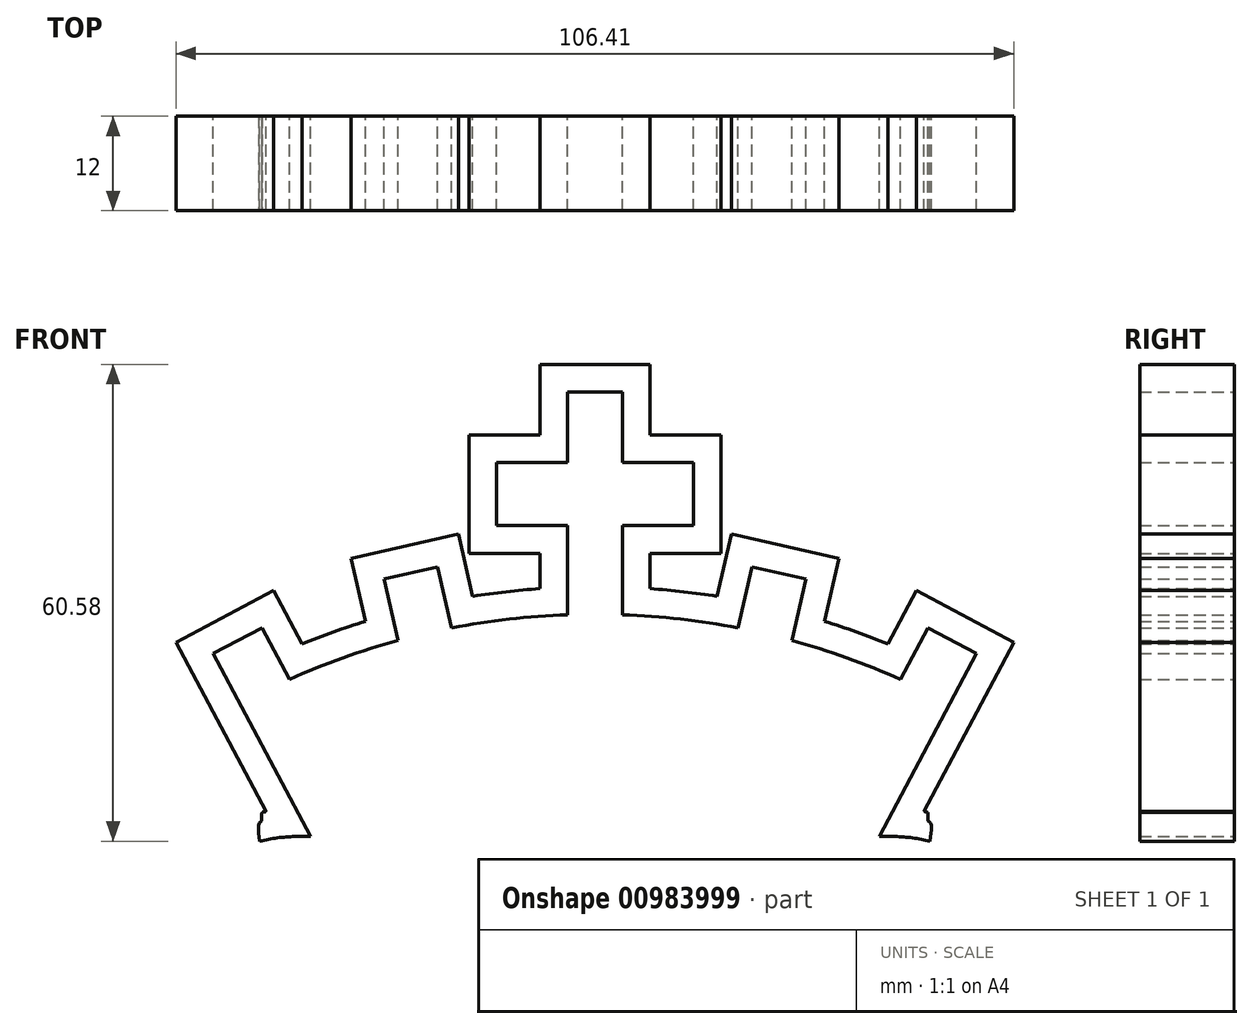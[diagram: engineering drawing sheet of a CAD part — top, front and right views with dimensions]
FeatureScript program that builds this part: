
annotation { "Feature Type Name" : "Feature", "Feature Type Description" : "" }
export const myFeature = defineFeature(function(context is Context, id is Id, definition is map)
    precondition{}
    {
        {
            var Q0;
            Q0=qCreatedBy(makeId("Front.planeOp"),FACE);
            var sketch = newSketch(context, id + "F0", { "sketchPlane" : qUnion([Q0])});
            skArc(sketch, "E0", {"start": v(-3.78, 138.48) * mm, "mid": v(-11.16, 137.94) * mm, "end": v(-18.47, 136.81) * mm});
            skLineSegment(sketch, "E1", {"start": v(-36.4, 110.33) * mm, "end": v(-48.76, 133.55) * mm});
            skLineSegment(sketch, "E2", {"start": v(-48.76, 133.55) * mm, "end": v(-42.58, 136.84) * mm});
            skLineSegment(sketch, "E3", {"start": v(-35.57, 123.66) * mm, "end": v(-28.38, 110.13) * mm});
            skLineSegment(sketch, "E4", {"start": v(-27.08, 143.02) * mm, "end": v(-25.29, 135.23) * mm});
            skLineSegment(sketch, "E5", {"start": v(-27.08, 143.02) * mm, "end": v(-20.25, 144.59) * mm});
            skLineSegment(sketch, "E6", {"start": v(-20.25, 144.59) * mm, "end": v(-18.47, 136.79) * mm});
            skLineSegment(sketch, "E7", {"start": v(-0.28, 0.67) * mm, "end": v(-0.28, 172.6) * mm, "construction": true});
            skLineSegment(sketch, "E8", {"start": v(-0.28, 166.8) * mm, "end": v(-3.78, 166.8) * mm});
            skLineSegment(sketch, "E9", {"start": v(-3.78, 166.8) * mm, "end": v(-3.78, 157.8) * mm});
            skLineSegment(sketch, "E10", {"start": v(-3.78, 157.8) * mm, "end": v(-12.78, 157.8) * mm});
            skLineSegment(sketch, "E11", {"start": v(-12.78, 157.8) * mm, "end": v(-12.78, 149.8) * mm});
            skLineSegment(sketch, "E12", {"start": v(-12.78, 149.8) * mm, "end": v(-3.78, 149.8) * mm});
            skLineSegment(sketch, "E13", {"start": v(-3.78, 149.8) * mm, "end": v(-3.78, 138.48) * mm});
            skLineSegment(sketch, "E14.MirrorCS", {"start": v(-0.28, 166.8) * mm, "end": v(3.22, 166.8) * mm});
            skLineSegment(sketch, "E15.MirrorCS", {"start": v(3.22, 166.8) * mm, "end": v(3.22, 157.8) * mm});
            skLineSegment(sketch, "E16.MirrorCS", {"start": v(3.22, 157.8) * mm, "end": v(12.22, 157.8) * mm});
            skLineSegment(sketch, "E17.MirrorCS", {"start": v(12.22, 157.8) * mm, "end": v(12.22, 149.8) * mm});
            skLineSegment(sketch, "E18.MirrorCS", {"start": v(12.22, 149.8) * mm, "end": v(3.22, 149.8) * mm});
            skLineSegment(sketch, "E19.MirrorCS", {"start": v(3.22, 149.8) * mm, "end": v(3.22, 138.48) * mm});
            skArc(sketch, "E20.MirrorCS", {"start": v(3.22, 138.48) * mm, "mid": v(10.6, 137.94) * mm, "end": v(17.9, 136.81) * mm});
            skLineSegment(sketch, "E21.MirrorCS", {"start": v(19.68, 144.59) * mm, "end": v(17.9, 136.79) * mm});
            skLineSegment(sketch, "E22.MirrorCS", {"start": v(26.5, 143.02) * mm, "end": v(19.68, 144.59) * mm});
            skLineSegment(sketch, "E23.MirrorCS", {"start": v(26.5, 143.02) * mm, "end": v(24.72, 135.23) * mm});
            skLineSegment(sketch, "E24.MirrorCS", {"start": v(42, 136.84) * mm, "end": v(38.52, 130.28) * mm});
            skLineSegment(sketch, "E25.MirrorCS", {"start": v(48.19, 133.55) * mm, "end": v(42, 136.84) * mm});
            skLineSegment(sketch, "E26.MirrorCS", {"start": v(35.84, 110.33) * mm, "end": v(48.19, 133.55) * mm});
            skArc(sketch, "E27.trimOffspring", {"start": v(-25.29, 135.23) * mm, "mid": v(-32.29, 133.02) * mm, "end": v(-39.09, 130.28) * mm});
            skArc(sketch, "E28.trimOffspring", {"start": v(24.72, 135.23) * mm, "mid": v(31.72, 133.02) * mm, "end": v(38.52, 130.28) * mm});
            skArc(sketch, "E29", {"start": v(-0.28, 131.03) * mm, "mid": v(-18.32, 129.25) * mm, "end": v(-35.57, 123.66) * mm});
            skArc(sketch, "E30.MirrorCS", {"start": v(-0.28, 131.03) * mm, "mid": v(17.76, 129.25) * mm, "end": v(35, 123.66) * mm});
            skPoint(sketch, "E31.orphan", {"position": v(38.52, 130.28) * mm});
            skLineSegment(sketch, "E32.trimOffspring", {"start": v(-42.58, 136.84) * mm, "end": v(-39.09, 130.28) * mm});
            skLineSegment(sketch, "E33.trimOffspring", {"start": v(35, 123.66) * mm, "end": v(26.95, 108.53) * mm});
            skPoint(sketch, "E34.orphan", {"position": v(-0.28, 138.53) * mm});
            skLineSegment(sketch, "E35.0", {"start": v(-53.49, 135) * mm, "end": v(-41.13, 141.57) * mm});
            skLineSegment(sketch, "E36.0", {"start": v(-42.05, 113.49) * mm, "end": v(-53.49, 135) * mm});
            skLineSegment(sketch, "E37.0", {"start": v(-41.13, 141.57) * mm, "end": v(-37.51, 134.76) * mm});
            skArc(sketch, "E38.0", {"start": v(-29.44, 137.66) * mm, "mid": v(-33.5, 136.3) * mm, "end": v(-37.51, 134.76) * mm});
            skLineSegment(sketch, "E39.0", {"start": v(-31.27, 145.65) * mm, "end": v(-29.44, 137.66) * mm});
            skLineSegment(sketch, "E40.0", {"start": v(-31.27, 145.65) * mm, "end": v(-17.62, 148.78) * mm});
            skLineSegment(sketch, "E41.0", {"start": v(-17.62, 148.78) * mm, "end": v(-15.8, 140.84) * mm});
            skArc(sketch, "E42.0", {"start": v(-7.28, 141.8) * mm, "mid": v(-11.55, 141.41) * mm, "end": v(-15.8, 140.84) * mm});
            skLineSegment(sketch, "E43.0", {"start": v(-7.28, 146.3) * mm, "end": v(-7.28, 141.8) * mm});
            skLineSegment(sketch, "E44.0", {"start": v(-16.28, 146.3) * mm, "end": v(-7.28, 146.3) * mm});
            skLineSegment(sketch, "E45.0", {"start": v(-16.28, 161.3) * mm, "end": v(-16.28, 146.3) * mm});
            skLineSegment(sketch, "E46.0", {"start": v(-7.28, 161.3) * mm, "end": v(-16.28, 161.3) * mm});
            skLineSegment(sketch, "E47.0", {"start": v(-7.28, 170.3) * mm, "end": v(-7.28, 161.3) * mm});
            skLineSegment(sketch, "E48.0", {"start": v(-0.28, 170.3) * mm, "end": v(-7.28, 170.3) * mm});
            skArc(sketch, "E49.trimOffspring", {"start": v(-33.92, 120.56) * mm, "mid": v(-34.03, 120.51) * mm, "end": v(-34.14, 120.46) * mm});
            skLineSegment(sketch, "E50.MirrorCS", {"start": v(-0.28, 170.3) * mm, "end": v(6.72, 170.3) * mm});
            skLineSegment(sketch, "E51.MirrorCS", {"start": v(6.72, 170.3) * mm, "end": v(6.72, 161.3) * mm});
            skLineSegment(sketch, "E52.MirrorCS", {"start": v(6.72, 161.3) * mm, "end": v(15.72, 161.3) * mm});
            skLineSegment(sketch, "E53.MirrorCS", {"start": v(15.72, 161.3) * mm, "end": v(15.72, 146.3) * mm});
            skLineSegment(sketch, "E54.MirrorCS", {"start": v(15.72, 146.3) * mm, "end": v(6.72, 146.3) * mm});
            skLineSegment(sketch, "E55.MirrorCS", {"start": v(6.72, 146.3) * mm, "end": v(6.72, 141.8) * mm});
            skArc(sketch, "E56.MirrorCS", {"start": v(6.72, 141.8) * mm, "mid": v(10.98, 141.41) * mm, "end": v(15.23, 140.84) * mm});
            skLineSegment(sketch, "E57.MirrorCS", {"start": v(17.05, 148.78) * mm, "end": v(15.23, 140.84) * mm});
            skLineSegment(sketch, "E58.MirrorCS", {"start": v(30.7, 145.65) * mm, "end": v(17.05, 148.78) * mm});
            skLineSegment(sketch, "E59.MirrorCS", {"start": v(30.7, 145.65) * mm, "end": v(28.87, 137.66) * mm});
            skArc(sketch, "E60.MirrorCS", {"start": v(28.87, 137.66) * mm, "mid": v(32.94, 136.3) * mm, "end": v(36.94, 134.76) * mm});
            skLineSegment(sketch, "E61.MirrorCS", {"start": v(52.92, 135) * mm, "end": v(40.56, 141.57) * mm});
            skLineSegment(sketch, "E62.MirrorCS", {"start": v(41.5, 113.5) * mm, "end": v(52.92, 135) * mm});
            skLineSegment(sketch, "E63.MirrorCS", {"start": v(40.56, 141.57) * mm, "end": v(36.94, 134.76) * mm});
            skLineSegment(sketch, "E64", {"start": v(-12.14, -7.37) * mm, "end": v(-12.14, 96.63) * mm, "construction": true});
            skArc(sketch, "E65.0", {"start": v(-10, 84.94) * mm, "mid": v(-10.03, 84.98) * mm, "end": v(-10.07, 85.02) * mm});
            skArc(sketch, "E66.MirrorCS", {"start": v(-14.28, 84.94) * mm, "mid": v(-14.24, 84.98) * mm, "end": v(-14.2, 85.02) * mm});
            skArc(sketch, "E67", {"start": v(42.44, 113.3) * mm, "mid": v(41.97, 113.4) * mm, "end": v(41.5, 113.5) * mm});
            skFitSpline(sketch, "E68", {"points": [v(42.44, 113.3) * mm, v(48.23, 111.53) * mm, v(55.7, 107.6) * mm, v(61.9, 101.5) * mm, v(65.92, 94.73) * mm, v(67.89, 88.83) * mm, v(69.36, 82.15) * mm, v(70.05, 71.83) * mm, v(69.46, 64.17) * mm, v(67.2, 54.54) * mm, v(62.19, 42.74) * mm, v(55.9, 33.02) * mm, v(44.9, 19.75) * mm, v(31.04, 6.98) * mm, v(20.62, -1.48) * mm, v(11.87, -7.76) * mm, v(11.57, -7.93) * mm, v(11.06, -7.84) * mm, v(11.06, -6.69) * mm, v(42.44, 111.78) * mm, v(42.07, 112.27) * mm, v(42.04, 112.96) * mm, v(42, 113.4) * mm, v(42.02, 113.4) * mm, v(42.44, 113.3) * mm]});
            skLineSegment(sketch, "E69", {"start": v(11.57, -7.93) * mm, "end": v(11.57, 102.3) * mm, "construction": true});
            skFitSpline(sketch, "E70", {"points": [v(11.57, 96.96) * mm, v(14.66, 99.97) * mm, v(17.84, 102.83) * mm, v(20.9, 105.19) * mm, v(23.75, 107) * mm, v(26.6, 108.39) * mm, v(32.08, 109.98) * mm, v(36.25, 110.33) * mm, v(39.73, 110.2) * mm, v(43.2, 109.5) * mm, v(47.3, 108.18) * mm, v(53.28, 105.19) * mm, v(57.3, 101.65) * mm, v(60.43, 97.55) * mm, v(63.42, 91.5) * mm, v(65.23, 85.87) * mm, v(66.76, 75.24) * mm, v(66.48, 65.24) * mm, v(64.46, 56.55) * mm, v(60.43, 47.24) * mm, v(57.24, 41.26) * mm, v(53.35, 35.29) * mm, v(46.05, 26.12) * mm, v(40, 19.65) * mm, v(33.61, 13.68) * mm, v(26.18, 7.28) * mm, v(17.8, 0.7) * mm, v(11.57, -3.96) * mm, v(11.2, -4) * mm, v(11.06, -3.8) * mm, v(11.16, -3.55) * mm, v(11.18, 96.29) * mm, v(11.2, 96.76) * mm, v(11.57, 96.96) * mm]});
            skFitSpline(sketch, "E71", {"points": [v(11.57, 87.27) * mm, v(13.7, 89.35) * mm, v(20.52, 95.56) * mm, v(25.84, 99.95) * mm, v(30.22, 102.23) * mm, v(36.24, 103.22) * mm, v(43.25, 102.52) * mm, v(48.62, 100) * mm, v(52.48, 96.5) * mm, v(56.1, 90.89) * mm, v(58.67, 83.12) * mm, v(59.5, 73.19) * mm, v(58.8, 63.37) * mm, v(55.29, 52.62) * mm, v(50.85, 44.32) * mm, v(45.41, 36.5) * mm, v(38.1, 27.9) * mm, v(27.88, 18.14) * mm, v(16.55, 8.56) * mm, v(11.57, 5) * mm, v(11.33, 5) * mm, v(11.2, 5.06) * mm, v(11.25, 5.16) * mm, v(11.3, 5.4) * mm, v(7.23, 76.2) * mm, v(11.57, 87.27) * mm]});
            skFitSpline(sketch, "E72", {"points": [v(11.57, 82.47) * mm, v(15.03, 85.77) * mm, v(22.3, 92.8) * mm, v(25.69, 95.77) * mm, v(30.98, 98.66) * mm, v(36.43, 99.74) * mm, v(40.73, 99.57) * mm, v(45.52, 97.75) * mm, v(48.08, 96.02) * mm, v(50.07, 94.2) * mm, v(52.21, 90.98) * mm, v(54.03, 86.43) * mm, v(54.94, 83.13) * mm, v(56.35, 75.03) * mm, v(56.02, 65.6) * mm, v(53.45, 56.77) * mm, v(49.98, 49.08) * mm, v(44.94, 41.48) * mm, v(38.74, 33.38) * mm, v(33.2, 27.43) * mm, v(27.1, 21.65) * mm, v(18.5, 14.21) * mm, v(14.29, 11.07) * mm, v(11.57, 9.09) * mm, v(10.93, 9.03) * mm, v(10.62, 9.66) * mm, v(10.34, 10.74) * mm, v(7.94, 68.18) * mm, v(11.57, 82.47) * mm]});
            skPoint(sketch, "E73.orphan", {"position": v(36.22, 111.03) * mm});
            skPoint(sketch, "E74.orphan", {"position": v(24.32, 111.03) * mm});
            skFitSpline(sketch, "E75.MirrorCS", {"points": [v(11.57, 82.47) * mm, v(8.11, 85.77) * mm, v(0.84, 92.8) * mm, v(-2.55, 95.77) * mm, v(-7.84, 98.66) * mm, v(-13.3, 99.74) * mm, v(-17.59, 99.57) * mm, v(-22.38, 97.75) * mm, v(-24.94, 96.02) * mm, v(-26.93, 94.2) * mm, v(-29.07, 90.98) * mm, v(-30.9, 86.43) * mm, v(-31.8, 83.13) * mm, v(-33.2, 75.03) * mm, v(-32.88, 65.6) * mm, v(-30.31, 56.77) * mm, v(-26.84, 49.08) * mm, v(-21.8, 41.48) * mm, v(-15.6, 33.38) * mm, v(-10.07, 27.43) * mm, v(-3.95, 21.65) * mm, v(4.64, 14.21) * mm, v(8.85, 11.07) * mm, v(11.57, 9.09) * mm, v(12.2, 9.03) * mm, v(12.52, 9.66) * mm, v(12.8, 10.74) * mm, v(15.2, 68.18) * mm, v(11.57, 82.47) * mm]});
            skFitSpline(sketch, "E76.MirrorCS", {"points": [v(11.57, 87.27) * mm, v(9.44, 89.35) * mm, v(2.62, 95.56) * mm, v(-2.7, 99.95) * mm, v(-7.08, 102.23) * mm, v(-13.1, 103.22) * mm, v(-20.1, 102.52) * mm, v(-25.49, 100) * mm, v(-29.34, 96.5) * mm, v(-32.96, 90.89) * mm, v(-35.54, 83.12) * mm, v(-36.35, 73.19) * mm, v(-35.65, 63.37) * mm, v(-32.15, 52.62) * mm, v(-27.7, 44.32) * mm, v(-22.27, 36.5) * mm, v(-14.97, 27.9) * mm, v(-4.74, 18.14) * mm, v(6.6, 8.56) * mm, v(11.57, 5) * mm, v(11.81, 5) * mm, v(11.93, 5.06) * mm, v(11.9, 5.16) * mm, v(11.84, 5.4) * mm, v(15.91, 76.2) * mm, v(11.57, 87.27) * mm]});
            skFitSpline(sketch, "E77.MirrorCS", {"points": [v(11.57, 96.96) * mm, v(8.48, 99.97) * mm, v(5.3, 102.83) * mm, v(2.24, 105.19) * mm, v(-0.6, 107) * mm, v(-3.45, 108.39) * mm, v(-8.94, 109.98) * mm, v(-13.11, 110.33) * mm, v(-16.6, 110.2) * mm, v(-20.06, 109.5) * mm, v(-24.16, 108.18) * mm, v(-30.14, 105.19) * mm, v(-34.17, 101.65) * mm, v(-37.3, 97.55) * mm, v(-40.28, 91.5) * mm, v(-42.09, 85.87) * mm, v(-43.62, 75.24) * mm, v(-43.34, 65.24) * mm, v(-41.32, 56.55) * mm, v(-37.3, 47.24) * mm, v(-34.1, 41.26) * mm, v(-30.2, 35.29) * mm, v(-22.91, 26.12) * mm, v(-16.87, 19.65) * mm, v(-10.47, 13.68) * mm, v(-3.04, 7.28) * mm, v(5.34, 0.7) * mm, v(11.57, -3.96) * mm, v(11.95, -4) * mm, v(12.08, -3.8) * mm, v(11.98, -3.55) * mm, v(11.96, 96.29) * mm, v(11.94, 96.76) * mm, v(11.57, 96.96) * mm]});
            skPoint(sketch, "E78.orphan", {"position": v(-0.28, 111.03) * mm});
            skFitSpline(sketch, "E79.MirrorCS", {"points": [v(-12.14, 96.96) * mm, v(-15.23, 99.97) * mm, v(-18.4, 102.83) * mm, v(-21.47, 105.19) * mm, v(-24.31, 107) * mm, v(-27.16, 108.39) * mm, v(-32.65, 109.98) * mm, v(-36.82, 110.33) * mm, v(-40.3, 110.2) * mm, v(-43.77, 109.5) * mm, v(-47.87, 108.18) * mm, v(-53.85, 105.19) * mm, v(-57.88, 101.65) * mm, v(-61, 97.55) * mm, v(-64, 91.5) * mm, v(-65.8, 85.87) * mm, v(-67.33, 75.24) * mm, v(-67.05, 65.24) * mm, v(-65.03, 56.55) * mm, v(-61, 47.24) * mm, v(-57.8, 41.26) * mm, v(-53.91, 35.29) * mm, v(-46.62, 26.12) * mm, v(-40.57, 19.65) * mm, v(-34.18, 13.68) * mm, v(-26.75, 7.28) * mm, v(-18.36, 0.7) * mm, v(-12.14, -3.96) * mm, v(-11.76, -4) * mm, v(-11.63, -3.8) * mm, v(-11.72, -3.55) * mm, v(-11.74, 96.29) * mm, v(-11.77, 96.76) * mm, v(-12.14, 96.96) * mm]});
            skFitSpline(sketch, "E80.MirrorCS", {"points": [v(-12.14, 87.27) * mm, v(-14.27, 89.35) * mm, v(-21.09, 95.56) * mm, v(-26.4, 99.95) * mm, v(-30.79, 102.23) * mm, v(-36.8, 103.22) * mm, v(-43.82, 102.52) * mm, v(-49.2, 100) * mm, v(-53.05, 96.5) * mm, v(-56.67, 90.89) * mm, v(-59.24, 83.12) * mm, v(-60.06, 73.19) * mm, v(-59.36, 63.37) * mm, v(-55.85, 52.62) * mm, v(-51.41, 44.32) * mm, v(-45.98, 36.5) * mm, v(-38.68, 27.9) * mm, v(-28.45, 18.14) * mm, v(-17.12, 8.56) * mm, v(-12.14, 5) * mm, v(-11.9, 5) * mm, v(-11.78, 5.06) * mm, v(-11.82, 5.16) * mm, v(-11.87, 5.4) * mm, v(-7.8, 76.2) * mm, v(-12.14, 87.27) * mm]});
            skFitSpline(sketch, "E81.MirrorCS", {"points": [v(-12.14, 82.47) * mm, v(-15.6, 85.77) * mm, v(-22.87, 92.8) * mm, v(-26.26, 95.77) * mm, v(-31.55, 98.66) * mm, v(-37, 99.74) * mm, v(-41.3, 99.57) * mm, v(-46.09, 97.75) * mm, v(-48.65, 96.02) * mm, v(-50.63, 94.2) * mm, v(-52.78, 90.98) * mm, v(-54.6, 86.43) * mm, v(-55.5, 83.13) * mm, v(-56.91, 75.03) * mm, v(-56.58, 65.6) * mm, v(-54.02, 56.77) * mm, v(-50.55, 49.08) * mm, v(-45.51, 41.48) * mm, v(-39.31, 33.38) * mm, v(-33.78, 27.43) * mm, v(-27.66, 21.65) * mm, v(-19.07, 14.21) * mm, v(-14.85, 11.07) * mm, v(-12.14, 9.09) * mm, v(-11.5, 9.03) * mm, v(-11.19, 9.66) * mm, v(-10.91, 10.74) * mm, v(-8.51, 68.18) * mm, v(-12.14, 82.47) * mm]});
            skFitSpline(sketch, "E82.MirrorCS", {"points": [v(-43, 113.3) * mm, v(-48.8, 111.53) * mm, v(-56.27, 107.6) * mm, v(-62.46, 101.5) * mm, v(-66.5, 94.73) * mm, v(-68.46, 88.83) * mm, v(-69.93, 82.15) * mm, v(-70.62, 71.83) * mm, v(-70.03, 64.17) * mm, v(-67.77, 54.54) * mm, v(-62.76, 42.74) * mm, v(-56.47, 33.02) * mm, v(-45.46, 19.75) * mm, v(-31.6, 6.98) * mm, v(-21.19, -1.48) * mm, v(-12.44, -7.76) * mm, v(-12.14, -7.93) * mm, v(-11.63, -7.84) * mm, v(-11.63, -6.69) * mm, v(-43, 111.78) * mm, v(-42.64, 112.27) * mm, v(-42.6, 112.96) * mm, v(-42.58, 113.4) * mm, v(-42.6, 113.4) * mm, v(-43, 113.3) * mm]});
            skPoint(sketch, "E83.orphan", {"position": v(0, 113.54) * mm});
            skArc(sketch, "E84", {"start": v(-42.05, 113.49) * mm, "mid": v(-42.32, 113.45) * mm, "end": v(-42.58, 113.4) * mm});
            skFitSpline(sketch, "E85.MirrorCS", {"points": [v(-12.14, 82.47) * mm, v(-8.68, 85.77) * mm, v(-1.4, 92.8) * mm, v(1.98, 95.77) * mm, v(7.27, 98.66) * mm, v(12.72, 99.74) * mm, v(17.02, 99.57) * mm, v(21.81, 97.75) * mm, v(24.37, 96.02) * mm, v(26.36, 94.2) * mm, v(28.5, 90.98) * mm, v(30.32, 86.43) * mm, v(31.23, 83.13) * mm, v(32.64, 75.03) * mm, v(32.3, 65.6) * mm, v(29.75, 56.77) * mm, v(26.27, 49.08) * mm, v(21.23, 41.48) * mm, v(15.04, 33.38) * mm, v(9.5, 27.43) * mm, v(3.39, 21.65) * mm, v(-5.2, 14.21) * mm, v(-9.42, 11.07) * mm, v(-12.14, 9.09) * mm, v(-12.78, 9.03) * mm, v(-13.09, 9.66) * mm, v(-13.37, 10.74) * mm, v(-15.76, 68.18) * mm, v(-12.14, 82.47) * mm]});
            skFitSpline(sketch, "E86.MirrorCS", {"points": [v(-12.14, 87.27) * mm, v(-10, 89.35) * mm, v(-3.19, 95.56) * mm, v(2.13, 99.95) * mm, v(6.51, 102.23) * mm, v(12.53, 103.22) * mm, v(19.54, 102.52) * mm, v(24.92, 100) * mm, v(28.77, 96.5) * mm, v(32.4, 90.89) * mm, v(34.97, 83.12) * mm, v(35.78, 73.19) * mm, v(35.08, 63.37) * mm, v(31.58, 52.62) * mm, v(27.14, 44.32) * mm, v(21.7, 36.5) * mm, v(14.4, 27.9) * mm, v(4.17, 18.14) * mm, v(-7.16, 8.56) * mm, v(-12.14, 5) * mm, v(-12.38, 5) * mm, v(-12.5, 5.06) * mm, v(-12.46, 5.16) * mm, v(-12.41, 5.4) * mm, v(-16.48, 76.2) * mm, v(-12.14, 87.27) * mm]});
            skFitSpline(sketch, "E87.MirrorCS", {"points": [v(-12.14, 96.96) * mm, v(-9.04, 99.97) * mm, v(-5.87, 102.83) * mm, v(-2.81, 105.19) * mm, v(0.04, 107) * mm, v(2.89, 108.39) * mm, v(8.38, 109.98) * mm, v(12.54, 110.33) * mm, v(16.02, 110.2) * mm, v(19.5, 109.5) * mm, v(23.6, 108.18) * mm, v(29.57, 105.19) * mm, v(33.6, 101.65) * mm, v(36.73, 97.55) * mm, v(39.71, 91.5) * mm, v(41.52, 85.87) * mm, v(43.05, 75.24) * mm, v(42.77, 65.24) * mm, v(40.76, 56.55) * mm, v(36.73, 47.24) * mm, v(33.53, 41.26) * mm, v(29.64, 35.29) * mm, v(22.34, 26.12) * mm, v(16.3, 19.65) * mm, v(9.9, 13.68) * mm, v(2.47, 7.28) * mm, v(-5.91, 0.7) * mm, v(-12.14, -3.96) * mm, v(-12.52, -4) * mm, v(-12.65, -3.8) * mm, v(-12.55, -3.55) * mm, v(-12.53, 96.29) * mm, v(-12.5, 96.76) * mm, v(-12.14, 96.96) * mm]});
            skLineSegment(sketch, "E88", {"start": v(-12.14, 96.96) * mm, "end": v(-12.14, 106.97) * mm, "construction": true});
            skFitSpline(sketch, "E89.trimOffspring", {"points": [v(18.73, 113.3) * mm, v(24.53, 111.53) * mm, v(32, 107.6) * mm, v(38.18, 101.5) * mm, v(42.21, 94.73) * mm, v(44.18, 88.83) * mm, v(45.65, 82.15) * mm, v(46.34, 71.83) * mm, v(45.75, 64.17) * mm, v(43.5, 54.54) * mm, v(38.48, 42.74) * mm, v(32.2, 33.02) * mm, v(21.18, 19.75) * mm, v(7.33, 6.98) * mm, v(-3.09, -1.48) * mm, v(-11.83, -7.76) * mm, v(-12.14, -7.93) * mm, v(-12.65, -7.84) * mm, v(-12.65, -6.69) * mm, v(18.73, 111.78) * mm, v(18.37, 112.27) * mm, v(18.33, 112.96) * mm, v(18.3, 113.4) * mm, v(18.31, 113.4) * mm, v(18.73, 113.3) * mm]});
            skFitSpline(sketch, "E90.trimOffspring", {"points": [v(-19.3, 113.3) * mm, v(-25.1, 111.53) * mm, v(-32.56, 107.6) * mm, v(-38.75, 101.5) * mm, v(-42.78, 94.73) * mm, v(-44.75, 88.83) * mm, v(-46.22, 82.15) * mm, v(-46.9, 71.83) * mm, v(-46.32, 64.17) * mm, v(-44.06, 54.54) * mm, v(-39.05, 42.74) * mm, v(-32.76, 33.02) * mm, v(-21.75, 19.75) * mm, v(-7.9, 6.98) * mm, v(2.52, -1.48) * mm, v(11.26, -7.76) * mm, v(11.57, -7.93) * mm, v(12.08, -7.84) * mm, v(12.08, -6.69) * mm, v(-19.3, 111.78) * mm, v(-18.93, 112.27) * mm, v(-18.9, 112.96) * mm, v(-18.87, 113.4) * mm, v(-18.88, 113.4) * mm, v(-19.3, 113.3) * mm]});
            skFitSpline(sketch, "E91.trimOffspring", {"points": [v(18.73, 113.3) * mm, v(24.53, 111.53) * mm, v(32, 107.6) * mm, v(38.18, 101.5) * mm, v(42.21, 94.73) * mm, v(44.18, 88.83) * mm, v(45.65, 82.15) * mm, v(46.34, 71.83) * mm, v(45.75, 64.17) * mm, v(43.5, 54.54) * mm, v(38.48, 42.74) * mm, v(32.2, 33.02) * mm, v(21.18, 19.75) * mm, v(7.33, 6.98) * mm, v(-3.09, -1.48) * mm, v(-11.83, -7.76) * mm, v(-12.14, -7.93) * mm, v(-12.65, -7.84) * mm, v(-12.65, -6.69) * mm, v(18.73, 111.78) * mm, v(18.37, 112.27) * mm, v(18.33, 112.96) * mm, v(18.3, 113.4) * mm, v(18.31, 113.4) * mm, v(18.73, 113.3) * mm]});
            skFitSpline(sketch, "E92.trimOffspring", {"points": [v(-19.3, 113.3) * mm, v(-25.1, 111.53) * mm, v(-32.56, 107.6) * mm, v(-38.75, 101.5) * mm, v(-42.78, 94.73) * mm, v(-44.75, 88.83) * mm, v(-46.22, 82.15) * mm, v(-46.9, 71.83) * mm, v(-46.32, 64.17) * mm, v(-44.06, 54.54) * mm, v(-39.05, 42.74) * mm, v(-32.76, 33.02) * mm, v(-21.75, 19.75) * mm, v(-7.9, 6.98) * mm, v(2.52, -1.48) * mm, v(11.26, -7.76) * mm, v(11.57, -7.93) * mm, v(12.08, -7.84) * mm, v(12.08, -6.69) * mm, v(-19.3, 111.78) * mm, v(-18.93, 112.27) * mm, v(-18.9, 112.96) * mm, v(-18.87, 113.4) * mm, v(-18.88, 113.4) * mm, v(-19.3, 113.3) * mm]});
            skArc(sketch, "E93.trimOffspring", {"start": v(-4.97, 108.93) * mm, "mid": v(-8.75, 106.3) * mm, "end": v(-12.14, 103.17) * mm});
            skArc(sketch, "E94.trimOffspring", {"start": v(19.48, 109.5) * mm, "mid": v(15.64, 106.64) * mm, "end": v(12.3, 103.2) * mm});
            skArc(sketch, "E95", {"start": v(26.95, 108.53) * mm, "mid": v(25.92, 108.13) * mm, "end": v(24.92, 107.64) * mm});
            skPoint(sketch, "E96.orphan", {"position": v(-24.9, 111.03) * mm});
            skArc(sketch, "E97", {"start": v(23.85, 111.77) * mm, "mid": v(11.68, 113.79) * mm, "end": v(-0.28, 110.75) * mm});
            skArc(sketch, "E98", {"start": v(-0.28, 110.75) * mm, "mid": v(-12.63, 113.8) * mm, "end": v(-25.15, 111.51) * mm});
            skPoint(sketch, "E99.orphan", {"position": v(-0.32, 127.53) * mm});
            skPoint(sketch, "E100.orphan", {"position": v(-0.25, 127.53) * mm});
            skArc(sketch, "E101", {"start": v(30.1, 121.92) * mm, "mid": v(-0.28, 127.53) * mm, "end": v(-30.68, 121.92) * mm});
            skLineSegment(sketch, "E102", {"start": v(-30.68, 121.92) * mm, "end": v(-25.15, 111.51) * mm});
            skLineSegment(sketch, "E103", {"start": v(30.1, 121.92) * mm, "end": v(24.95, 112.2) * mm});
            skArc(sketch, "E104", {"start": v(24.95, 112.2) * mm, "mid": v(24.37, 112.07) * mm, "end": v(23.85, 111.77) * mm});
            skSolve(sketch);
        }
        {
            var Q0;
            {var subQ13=sQuery(id+"F0.wireOp",EDGE,"E0");Q0=makeQuery(id+"F0.imprint","IMPRINT",FACE,{"disambiguationData":[TD([[makeQuery(id+"F0.imprint","IMPRINT",EDGE,{"derivedFrom":subQ13}),-1.0]])]});}
            extrude(context, id + "F1", {"entities" : qUnion([Q0]), "endBound" : BoundingType.SYMMETRIC, "depth" : 12 * mm, "offsetDistance" : 25 * mm});
        }
    });
